# Revit family: VRSCS
name_source: partatom
category: Lighting Fixtures
units: mm (PartAtom-declared; Revit-internal decimal feet)

## family parameters
Always vertical = Yes
Cut with Voids When Loaded = No
Host = Ceiling
Light Source = Yes
Maintain Annotation Orientation = No
OmniClass Number = 23.80.70.11
OmniClass Title = Luminaries for Internal Lighting
Part Type = Normal
Room Calculation Point = No
Round Connector Dimension = Use Diameter
Shared = No

## types (15) — shared parameters
Assembly Code = D5020200
Color Filter = 16777215
Default Elevation = 0' - 0"
Description = LED Surface Mount Correctional Clamshell with Sloped Sides
Dimming Lamp Color Temperature Shift = <None>
Emit Shape Visible in Rendering = No
Housing Finish = Metal - Viscor - White
Lamp = LED
Lens Finish = Polycarbonate - Viscor - Frosted Prismatic P12
Manufacturer = CERTOLUX by VISCOR
Model = VRSCS
Tilt Angle = 90.00°
URL = https://viscor.com
Voltage = 120 V

## per-type parameters (varying)
| type | Apparent Load | Emit from Rectangle Length | Emit from Rectangle Width | Lamp Wattage | Length | Lens Frame Length | Lens Frame Width | Lens Length | Lens Width | Photometric Web File | Width |
| VRSCS-2X2-LED840K026LUNV | 25 VA | 2' - 0" | 2' - 0" | 25 VA | 2' - 0" | 1' - 7" | 1' - 7" | 1' - 8" | 1' - 8" | VRSCS-2X2-LED840K026LUNV.ies | 2' - 0" |
| VRSCS-2X4-LED840K052LUNV | 49 VA | 2' - 0" | 4' - 0" | 49 VA | 4' - 0" | 3' - 7" | 1' - 7" | 3' - 8" | 1' - 8" | VRSCS-2X4-LED840K052LUNV.ies | 2' - 0" |
| VRSCS-2X2-LED840K052LUNV | 52 VA | 2' - 0" | 2' - 0" | 52 VA | 2' - 0" | 1' - 7" | 1' - 7" | 1' - 8" | 1' - 8" | VRSCS-2X2-LED840K052LUNV.ies | 2' - 0" |
| VRSCS-2X2-LED840K078LUNV | 77 VA | 2' - 0" | 2' - 0" | 77 VA | 2' - 0" | 1' - 7" | 1' - 7" | 1' - 8" | 1' - 8" | VRSCS-2X2-LED840K078LUNV.ies | 2' - 0" |
| VRSCS-2X2-LED840K104LUNV | 107 VA | 2' - 0" | 2' - 0" | 107 VA | 2' - 0" | 1' - 7" | 1' - 7" | 1' - 8" | 1' - 8" | VRSCS-2X2-LED840K104LUNV.ies | 2' - 0" |
| VRSCS-2X4-LED840K078LUNV | 75 VA | 2' - 0" | 4' - 0" | 75 VA | 4' - 0" | 3' - 7" | 1' - 7" | 3' - 8" | 1' - 8" | VRSCS-2X4-LED840K078LUNV.ies | 2' - 0" |
| VRSCS-2X4-LED840K104LUNV | 102 VA | 2' - 0" | 4' - 0" | 102 VA | 4' - 0" | 3' - 7" | 1' - 7" | 3' - 8" | 1' - 8" | VRSCS-2X4-LED840K104LUNV.ies | 2' - 0" |
| VRSCS-2X4-LED840K150LUNV | 149 VA | 2' - 0" | 4' - 0" | 149 VA | 4' - 0" | 3' - 7" | 1' - 7" | 3' - 8" | 1' - 8" | VRSCS-2X4-LED840K150LUNV.ies | 2' - 0" |
| VRSCS-1X4-LED840K026LUNV | 25 VA | 1' - 0" | 4' - 0" | 25 VA | 4' - 0" | 3' - 7" | 0' - 7" | 3' - 8" | 0' - 8" | VRSCS-1X4-LED840K026LUNV.ies | 1' - 0" |
| VRSCS-1X4-LED840K052LUNV | 52 VA | 1' - 0" | 4' - 0" | 52 VA | 4' - 0" | 3' - 7" | 0' - 7" | 3' - 8" | 0' - 8" | VRSCS-1X4-LED840K052LUNV.ies | 1' - 0" |
| VRSCS-1X4-LED840K078LUNV | 77 VA | 1' - 0" | 4' - 0" | 77 VA | 4' - 0" | 3' - 7" | 0' - 7" | 3' - 8" | 0' - 8" | VRSCS-1X4-LED840K078LUNV.ies | 1' - 0" |
| VRSCS-1X4-LED840K104LUNV | 107 VA | 1' - 0" | 4' - 0" | 107 VA | 4' - 0" | 3' - 7" | 0' - 7" | 3' - 8" | 0' - 8" | VRSCS-1X4-LED840K104LUNV.ies | 1' - 0" |
| VRSCS-1X2-LED840K026LUNV | 27 VA | 1' - 0" | 2' - 0" | 27 VA | 2' - 0" | 1' - 7" | 0' - 7" | 1' - 8" | 0' - 8" | VRSCS-1X2-LED840K026LUNV.ies | 1' - 0" |
| VRSCS-1X2-LED840K036LUNV | 36 VA | 1' - 0" | 2' - 0" | 36 VA | 2' - 0" | 1' - 7" | 0' - 7" | 1' - 8" | 0' - 8" | VRSCS-1X2-LED840K036LUNV.ies | 1' - 0" |
| VRSCS-1X2-LED840K052LUNV | 54 VA | 1' - 0" | 2' - 0" | 54 VA | 2' - 0" | 1' - 7" | 0' - 7" | 1' - 8" | 0' - 8" | VRSCS-1X2-LED840K052LUNV.ies | 1' - 0" |

## geometry (parser evidence)
native form markers: Sweep x3
no freeform markers — native parametric forms only
